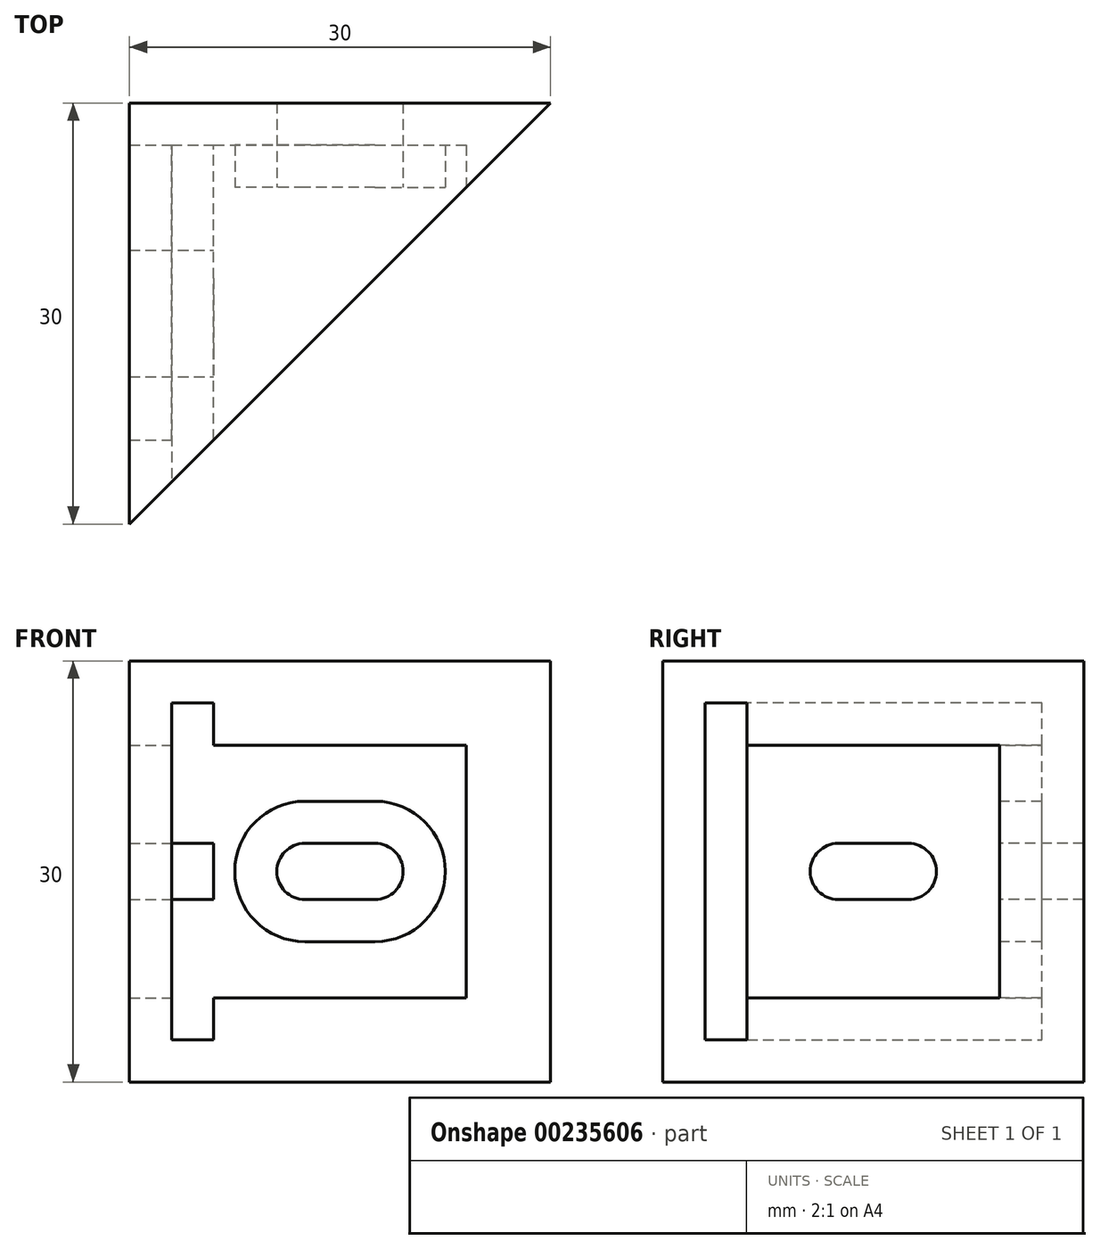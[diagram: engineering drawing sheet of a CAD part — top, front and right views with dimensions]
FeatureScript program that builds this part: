
annotation { "Feature Type Name" : "Feature", "Feature Type Description" : "" }
export const myFeature = defineFeature(function(context is Context, id is Id, definition is map)
    precondition{}
    {
        {
            var Q0;
            Q0=qCreatedBy(makeId("Top.planeOp"),FACE);
            var sketch = newSketch(context, id + "F0", { "sketchPlane" : qUnion([Q0])});
            skLineSegment(sketch, "E0", {"start": v(0, 0) * mm, "end": v(0, 30) * mm});
            skLineSegment(sketch, "E1", {"start": v(0, 30) * mm, "end": v(30, 30) * mm});
            skLineSegment(sketch, "E2", {"start": v(30, 30) * mm, "end": v(0, 0) * mm});
            skSolve(sketch);
        }
        {
            var Q0;
            Q0 = qSketchRegion(id + "F0", true);
            extrude(context, id + "F1", {"entities" : qUnion([Q0]), "depth" : 30 * mm, "offsetDistance" : 25 * mm});
        }
        {
            var Q0;
            Q0=makeQuery(id+"F1.opExtrude","SWEPT_FACE",FACE,{"disambiguationData":[OSD([sQuery(id+"F0.wireOp",EDGE,"E2")])]});
            shell(context, id + "F2", {"entities" : qUnion([Q0]), "thickness" : 6 * mm});
        }
        {
            var Q0;
            Q0=makeQuery(id+"F2.opShell","OFFSET_FACE",FACE,{"disambiguationData":[OSD([sQuery(id+"F0.wireOp",EDGE,"E1")])]});
            var sketch = newSketch(context, id + "F3", { "sketchPlane" : qUnion([Q0])});
            skLineSegment(sketch, "E3", {"start": v(6, 24) * mm, "end": v(24, 6) * mm, "construction": true});
            skLineSegment(sketch, "E4", {"start": v(17.5, 15) * mm, "end": v(12.5, 15) * mm, "construction": true});
            skPoint(sketch, "E4.startSnap0", {"position": v(15, 15) * mm});
            skArc(sketch, "E5.0.startCap", {"start": v(17.5, 17) * mm, "mid": v(19.5, 15) * mm, "end": v(17.5, 13) * mm});
            skArc(sketch, "E5.0.endCap", {"start": v(12.5, 13) * mm, "mid": v(10.5, 15) * mm, "end": v(12.5, 17) * mm});
            skLineSegment(sketch, "E5.0.left", {"start": v(17.5, 13) * mm, "end": v(12.5, 13) * mm});
            skLineSegment(sketch, "E5.0.right", {"start": v(17.5, 17) * mm, "end": v(12.5, 17) * mm});
            skSolve(sketch);
        }
        {
            var Q0;
            Q0 = qSketchRegion(id + "F3", true);
            extrude(context, id + "F4", {"entities" : qUnion([Q0]), "operationType" : NewBodyOperationType.REMOVE, "endBound" : BoundingType.THROUGH_ALL, "oppositeDirection" : true, "depth" : 25 * mm, "offsetDistance" : 25 * mm});
        }
        {
            var Q0;
            Q0=makeQuery(id+"F2.opShell","OFFSET_FACE",FACE,{"disambiguationData":[OSD([sQuery(id+"F0.wireOp",EDGE,"E1")])]});
            var sketch = newSketch(context, id + "F5", { "sketchPlane" : qUnion([Q0])});
            skArc(sketch, "E6.0", {"start": v(17.5, 20) * mm, "mid": v(22.5, 15) * mm, "end": v(17.5, 10) * mm});
            skLineSegment(sketch, "E6.1", {"start": v(17.5, 20) * mm, "end": v(12.5, 20) * mm});
            skArc(sketch, "E6.2", {"start": v(12.5, 10) * mm, "mid": v(7.5, 15) * mm, "end": v(12.5, 20) * mm});
            skLineSegment(sketch, "E6.3", {"start": v(17.5, 10) * mm, "end": v(12.5, 10) * mm});
            skSolve(sketch);
        }
        {
            var Q0;
            Q0=makeQuery(id+"F5.imprint","IMPRINT",FACE,{"disambiguationData":[TD([[makeQuery(id+"F5.imprint","IMPRINT",EDGE,{"derivedFrom":sQuery(id+"F5.wireOp",EDGE,"E6.0")}),-1.0]])]});
            extrude(context, id + "F6", {"entities" : qUnion([Q0]), "operationType" : NewBodyOperationType.REMOVE, "oppositeDirection" : true, "depth" : 3 * mm, "offsetDistance" : 25 * mm});
        }
        {
            var Q0;
            Q0=makeQuery(id+"F2.opShell","OFFSET_FACE",FACE,{"disambiguationData":[OSD([sQuery(id+"F0.wireOp",EDGE,"E0")])]});
            var sketch = newSketch(context, id + "F7", { "sketchPlane" : qUnion([Q0])});
            skLineSegment(sketch, "E7", {"start": v(6, 24) * mm, "end": v(24, 6) * mm, "construction": true});
            skLineSegment(sketch, "E8", {"start": v(17.5, 15) * mm, "end": v(12.5, 15) * mm, "construction": true});
            skPoint(sketch, "E9", {"position": v(15, 15) * mm});
            skArc(sketch, "E10.0.startCap", {"start": v(17.5, 17) * mm, "mid": v(19.5, 15) * mm, "end": v(17.5, 13) * mm});
            skArc(sketch, "E10.0.endCap", {"start": v(12.5, 13) * mm, "mid": v(10.5, 15) * mm, "end": v(12.5, 17) * mm});
            skLineSegment(sketch, "E10.0.left", {"start": v(17.5, 13) * mm, "end": v(12.5, 13) * mm});
            skLineSegment(sketch, "E10.0.right", {"start": v(17.5, 17) * mm, "end": v(12.5, 17) * mm});
            skSolve(sketch);
        }
        {
            var Q0;
            Q0=makeQuery(id+"F7.imprint","IMPRINT",FACE,{"disambiguationData":[TD([[makeQuery(id+"F7.imprint","IMPRINT",EDGE,{"derivedFrom":sQuery(id+"F7.wireOp",EDGE,"E10.0.startCap")}),-1.0]])]});
            extrude(context, id + "F8", {"entities" : qUnion([Q0]), "operationType" : NewBodyOperationType.REMOVE, "endBound" : BoundingType.THROUGH_ALL, "oppositeDirection" : true, "depth" : 25 * mm, "offsetDistance" : 25 * mm});
        }
        {
            var Q0;
            Q0=makeQuery(id+"F2.opShell","OFFSET_FACE",FACE,{"disambiguationData":[OSD([sQuery(id+"F0.wireOp",EDGE,"E0")])]});
            var sketch = newSketch(context, id + "F9", { "sketchPlane" : qUnion([Q0])});
            skLineSegment(sketch, "E11.0", {"start": v(3, 3) * mm, "end": v(27, 3) * mm});
            skLineSegment(sketch, "E11.1", {"start": v(3, 27) * mm, "end": v(3, 3) * mm});
            skLineSegment(sketch, "E11.2", {"start": v(27, 27) * mm, "end": v(3, 27) * mm});
            skLineSegment(sketch, "E11.3", {"start": v(27, 3) * mm, "end": v(27, 27) * mm});
            skArc(sketch, "E12.0", {"start": v(12.5, 10) * mm, "mid": v(7.5, 15) * mm, "end": v(12.5, 20) * mm});
            skLineSegment(sketch, "E12.1", {"start": v(17.5, 10) * mm, "end": v(12.5, 10) * mm});
            skArc(sketch, "E12.2", {"start": v(17.5, 20) * mm, "mid": v(22.5, 15) * mm, "end": v(17.5, 10) * mm});
            skLineSegment(sketch, "E12.3", {"start": v(17.5, 20) * mm, "end": v(12.5, 20) * mm});
            skSolve(sketch);
        }
        {
            var Q0;
            Q0=makeQuery(id+"F9.imprint","IMPRINT",FACE,{"disambiguationData":[TD([[makeQuery(id+"F9.imprint","IMPRINT",EDGE,{"derivedFrom":sQuery(id+"F9.wireOp",EDGE,"E12.0")}),-1.0]])]});
            extrude(context, id + "F10", {"entities" : qUnion([Q0]), "operationType" : NewBodyOperationType.REMOVE, "oppositeDirection" : true, "depth" : 3 * mm, "offsetDistance" : 25 * mm});
        }
    });
